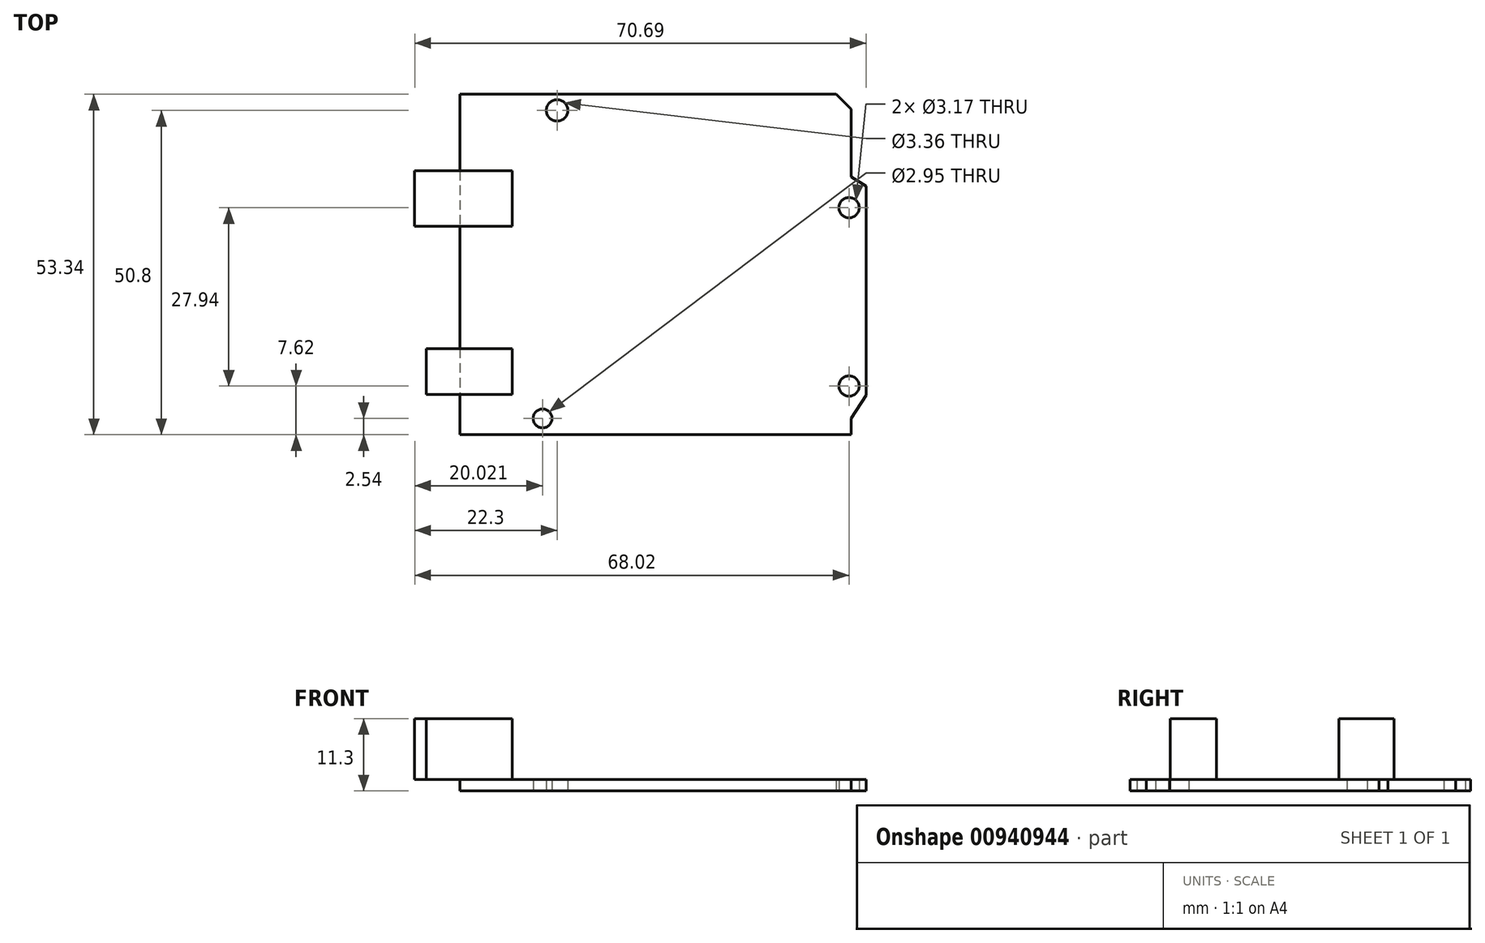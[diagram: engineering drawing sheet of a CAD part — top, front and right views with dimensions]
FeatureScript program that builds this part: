
annotation { "Feature Type Name" : "Feature", "Feature Type Description" : "" }
export const myFeature = defineFeature(function(context is Context, id is Id, definition is map)
    precondition{}
    {
        {
            var Q0;
            Q0=qCreatedBy(makeId("Top.planeOp"),FACE);
            var sketch = newSketch(context, id + "F0", { "sketchPlane" : qUnion([Q0])});
            skLineSegment(sketch, "E0", {"start": v(0, 0) * mm, "end": v(61.27, 0) * mm});
            skLineSegment(sketch, "E1", {"start": v(61.27, 0) * mm, "end": v(61.27, 2.54) * mm});
            skLineSegment(sketch, "E2", {"start": v(0, 53.34) * mm, "end": v(58.91, 53.34) * mm});
            skLineSegment(sketch, "E3", {"start": v(61.27, 50.98) * mm, "end": v(61.27, 40.38) * mm});
            skLineSegment(sketch, "E4", {"start": v(58.91, 53.34) * mm, "end": v(61.27, 50.98) * mm});
            skPoint(sketch, "E5", {"position": v(63.63, 38.97) * mm});
            skLineSegment(sketch, "E6", {"start": v(61.27, 40.38) * mm, "end": v(63.63, 38.97) * mm});
            skCircle(sketch, "E7", {"center": v(12.96, 2.54) * mm, "radius": 1.47 * mm});
            skCircle(sketch, "E8", {"center": v(15.24, 50.8) * mm, "radius": 1.68 * mm});
            skLineSegment(sketch, "E9", {"start": v(63.63, 38.97) * mm, "end": v(63.63, 6.2) * mm});
            skLineSegment(sketch, "E10", {"start": v(63.63, 6.2) * mm, "end": v(61.27, 2.54) * mm});
            skCircle(sketch, "E11", {"center": v(60.96, 35.56) * mm, "radius": 1.59 * mm});
            skCircle(sketch, "E12", {"center": v(60.96, 7.62) * mm, "radius": 1.59 * mm});
            skPoint(sketch, "E13.start.orphan", {"position": v(10.6, 2.95) * mm});
            skLineSegment(sketch, "E14", {"start": v(0, 53.34) * mm, "end": v(0, 0) * mm});
            skSolve(sketch);
        }
        {
            var Q0;
            Q0=qSketchRegion(id+"F0",true);
            extrude(context, id + "F1", {"entities" : qUnion([Q0]), "depth" : 1.78 * mm});
        }
        {
            var Q0;
            Q0=makeQuery(id+"F1.opExtrude","CAP_FACE",FACE,{"disambiguationData":[OSD([sQuery(id+"F0.wireOp",EDGE,"E0"),sQuery(id+"F0.wireOp",EDGE,"E1"),sQuery(id+"F0.wireOp",EDGE,"E2"),sQuery(id+"F0.wireOp",EDGE,"E3"),sQuery(id+"F0.wireOp",EDGE,"E4"),sQuery(id+"F0.wireOp",EDGE,"E6"),sQuery(id+"F0.wireOp",EDGE,"E7"),sQuery(id+"F0.wireOp",EDGE,"E8"),sQuery(id+"F0.wireOp",EDGE,"E9"),sQuery(id+"F0.wireOp",EDGE,"E10"),sQuery(id+"F0.wireOp",EDGE,"E11"),sQuery(id+"F0.wireOp",EDGE,"E12"),sQuery(id+"F0.wireOp",EDGE,"E14")])],"isStart":false});
            var sketch = newSketch(context, id + "F2", { "sketchPlane" : qUnion([Q0])});
            skLineSegment(sketch, "E15.bottom", {"start": v(8.2, 41.34) * mm, "end": v(-7.06, 41.34) * mm});
            skLineSegment(sketch, "E15.top", {"start": v(8.2, 32.67) * mm, "end": v(-7.06, 32.67) * mm});
            skLineSegment(sketch, "E15.left", {"start": v(8.2, 41.34) * mm, "end": v(8.2, 32.67) * mm});
            skLineSegment(sketch, "E15.right", {"start": v(-7.06, 41.34) * mm, "end": v(-7.06, 32.67) * mm});
            skLineSegment(sketch, "E16.bottom", {"start": v(8.2, 13.5) * mm, "end": v(-5.23, 13.5) * mm});
            skLineSegment(sketch, "E16.top", {"start": v(8.2, 6.28) * mm, "end": v(-5.23, 6.28) * mm});
            skLineSegment(sketch, "E16.left", {"start": v(8.2, 13.5) * mm, "end": v(8.2, 6.28) * mm});
            skLineSegment(sketch, "E16.right", {"start": v(-5.23, 13.5) * mm, "end": v(-5.23, 6.28) * mm});
            skSolve(sketch);
        }
        {
            var Q0;
            {var subQ0=sQuery(id+"F2.wireOp",EDGE,"E15.right");Q0=makeQuery(id+"F2.imprint","IMPRINT",FACE,{"disambiguationData":[TD([[makeQuery(id+"F2.imprint","IMPRINT",EDGE,{"derivedFrom":subQ0}),1.0]])]});}
            var Q1;
            {var subQ0=sQuery(id+"F2.wireOp",EDGE,"E16.right");Q1=makeQuery(id+"F2.imprint","IMPRINT",FACE,{"disambiguationData":[TD([[makeQuery(id+"F2.imprint","IMPRINT",EDGE,{"derivedFrom":subQ0}),1.0]])]});}
            var Q2;
            {var subQ0=sQuery(id+"F2.wireOp",EDGE,"E15.left");Q2=makeQuery(id+"F2.imprint","IMPRINT",FACE,{"disambiguationData":[TD([[makeQuery(id+"F2.imprint","IMPRINT",EDGE,{"derivedFrom":subQ0}),-1.0]])]});}
            var Q3;
            {var subQ0=sQuery(id+"F2.wireOp",EDGE,"E16.left");Q3=makeQuery(id+"F2.imprint","IMPRINT",FACE,{"disambiguationData":[TD([[makeQuery(id+"F2.imprint","IMPRINT",EDGE,{"derivedFrom":subQ0}),-1.0]])]});}
            extrude(context, id + "F3", {"entities" : qUnion([Q0, Q1, Q2, Q3]), "depth" : 9.52 * mm});
        }
        {
            var Q0;
            Q0=makeQuery(id+"F0.imprint","IMPRINT",FACE,{"disambiguationData":[TD([[makeQuery(id+"F0.imprint","IMPRINT",EDGE,{"derivedFrom":sQuery(id+"F0.wireOp",EDGE,"E0")}),1.0]])]});
            cPlane(context, id + "F4", {"entities" : qUnion([Q0]), "cplaneType" : CPlaneType.OFFSET, "offset" : 5 * mm, "oppositeDirection" : true, "width" : 152.4 * mm, "height" : 152.4 * mm});
        }
    });
